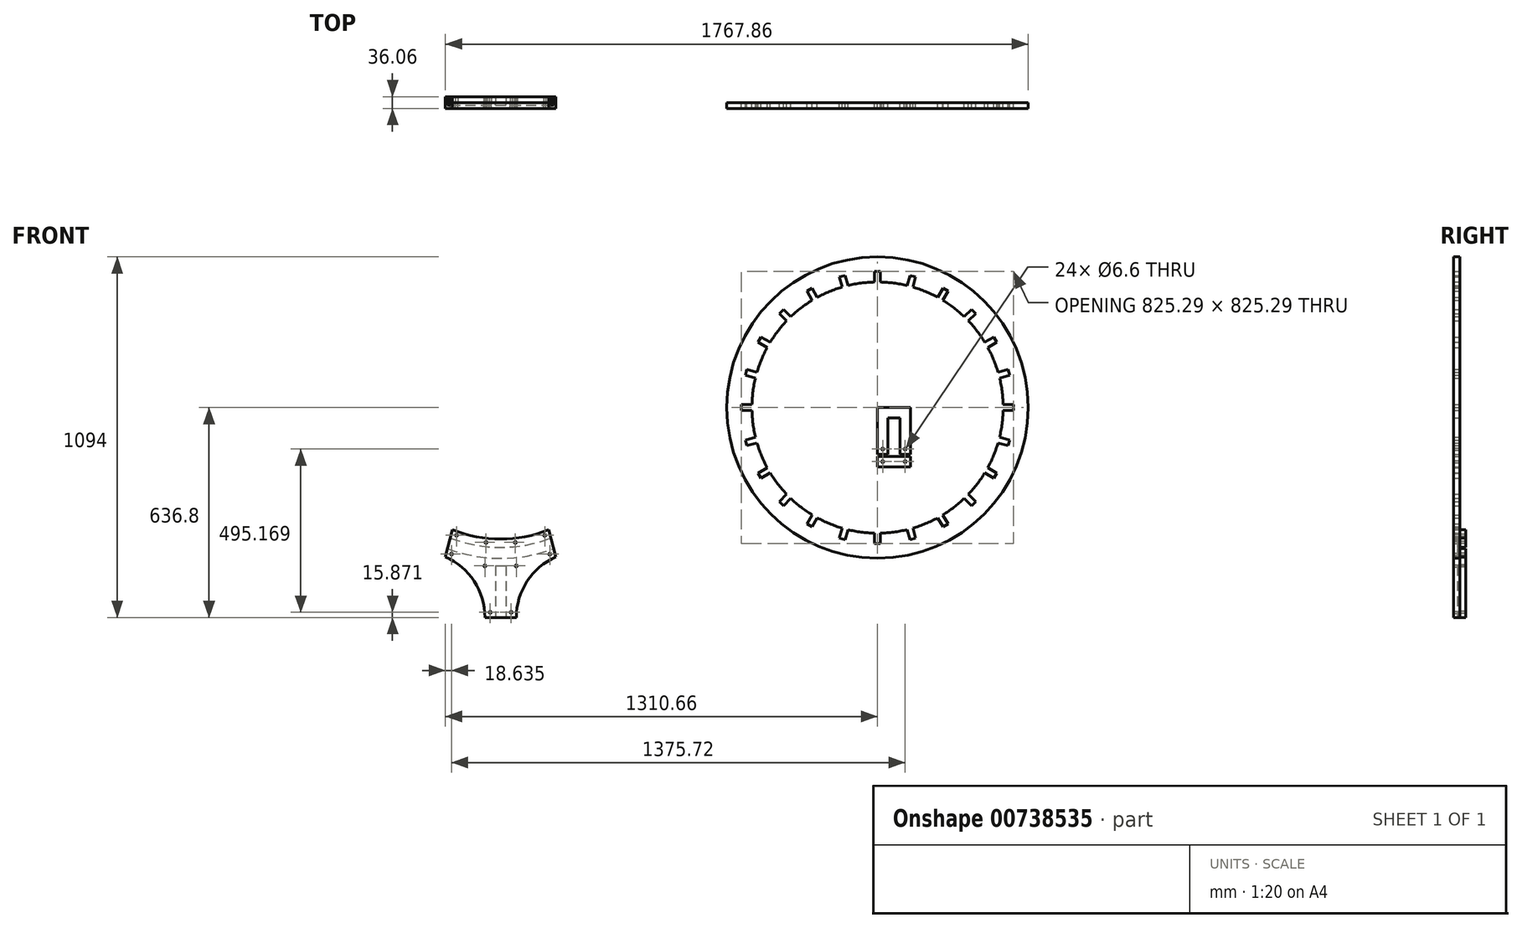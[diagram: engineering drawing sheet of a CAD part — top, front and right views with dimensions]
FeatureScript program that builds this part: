
annotation { "Feature Type Name" : "Feature", "Feature Type Description" : "" }
export const myFeature = defineFeature(function(context is Context, id is Id, definition is map)
    precondition{}
    {
        {
            var Q0;
            Q0=qCreatedBy(makeId("Front.planeOp"),FACE);
            var sketch = newSketch(context, id + "F0", { "sketchPlane" : qUnion([Q0])});
            skLineSegment(sketch, "E0.bottom", {"start": v(-15.88, -456.92) * mm, "end": v(15.87, -456.92) * mm, "construction": true});
            skLineSegment(sketch, "E0.top", {"start": v(-15.87, -660.12) * mm, "end": v(15.88, -660.12) * mm, "construction": true});
            skLineSegment(sketch, "E0.left", {"start": v(-15.87, -456.92) * mm, "end": v(-15.87, -660.12) * mm, "construction": true});
            skLineSegment(sketch, "E0.right", {"start": v(15.88, -456.92) * mm, "end": v(15.88, -660.12) * mm, "construction": true});
            skPoint(sketch, "E0.middle", {"position": v(0, -558.52) * mm});
            skLineSegment(sketch, "E1", {"start": v(-152.4, -395.59) * mm, "end": v(152.4, -395.59) * mm, "construction": true});
            skPoint(sketch, "E2", {"position": v(0, -395.59) * mm});
            skLineSegment(sketch, "E3", {"start": v(-152.4, -395.59) * mm, "end": v(-161.06, -427.9) * mm});
            skLineSegment(sketch, "E4", {"start": v(0, -395.59) * mm, "end": v(0, -457.2) * mm, "construction": true});
            skLineSegment(sketch, "E5.MirrorCS", {"start": v(152.4, -395.59) * mm, "end": v(161.06, -427.9) * mm});
            skArc(sketch, "E6", {"start": v(152.4, -395.59) * mm, "mid": v(0, 423.93) * mm, "end": v(-152.4, -395.59) * mm, "construction": true});
            skArc(sketch, "E7", {"start": v(-152.4, -395.59) * mm, "mid": v(-118.62, -407) * mm, "end": v(-84, -415.52) * mm});
            skArc(sketch, "E8", {"start": v(-161.06, -427.9) * mm, "mid": v(-126.24, -439.43) * mm, "end": v(-90.6, -448.13) * mm});
            skArc(sketch, "E9", {"start": v(161.06, -427.9) * mm, "mid": v(0, 457.2) * mm, "end": v(-161.06, -427.9) * mm, "construction": true});
            skArc(sketch, "E10.0", {"start": v(-145.79, -370.9) * mm, "mid": v(0, -398.53) * mm, "end": v(145.79, -370.9) * mm});
            skArc(sketch, "E11.0", {"start": v(-167.66, -452.54) * mm, "mid": v(0, -482.6) * mm, "end": v(167.66, -452.54) * mm, "construction": true});
            skLineSegment(sketch, "E12", {"start": v(-161.06, -427.9) * mm, "end": v(-167.66, -452.54) * mm});
            skLineSegment(sketch, "E13", {"start": v(-152.4, -395.59) * mm, "end": v(-145.79, -370.9) * mm});
            skLineSegment(sketch, "E14.MirrorCS", {"start": v(152.4, -395.59) * mm, "end": v(145.79, -370.9) * mm});
            skLineSegment(sketch, "E15.MirrorCS", {"start": v(161.06, -427.9) * mm, "end": v(167.66, -452.54) * mm});
            skLineSegment(sketch, "E16.bottom", {"start": v(-47.63, -480.24) * mm, "end": v(47.62, -480.24) * mm, "construction": true});
            skLineSegment(sketch, "E16.top", {"start": v(-47.63, -636.8) * mm, "end": v(-15.87, -636.8) * mm});
            skLineSegment(sketch, "E16.left", {"start": v(-47.63, -480.24) * mm, "end": v(-47.63, -636.8) * mm, "construction": true});
            skLineSegment(sketch, "E16.right", {"start": v(47.62, -480.24) * mm, "end": v(47.62, -636.8) * mm, "construction": true});
            skArc(sketch, "E17", {"start": v(-47.62, -636.8) * mm, "mid": v(-80.28, -526.85) * mm, "end": v(-167.66, -452.54) * mm});
            skArc(sketch, "E18.MirrorCS", {"start": v(47.62, -636.8) * mm, "mid": v(80.28, -526.85) * mm, "end": v(167.66, -452.54) * mm});
            skLineSegment(sketch, "E19.bottom", {"start": v(-15.87, -480.24) * mm, "end": v(15.88, -480.24) * mm});
            skLineSegment(sketch, "E19.top", {"start": v(-15.87, -636.8) * mm, "end": v(15.88, -636.8) * mm});
            skLineSegment(sketch, "E19.left", {"start": v(-15.87, -480.24) * mm, "end": v(-15.87, -636.8) * mm});
            skLineSegment(sketch, "E19.right", {"start": v(15.88, -480.24) * mm, "end": v(15.88, -636.8) * mm});
            skArc(sketch, "E20", {"start": v(-84, -415.52) * mm, "mid": v(35.62, -422.43) * mm, "end": v(152.4, -395.59) * mm});
            skArc(sketch, "E21", {"start": v(-90.6, -448.13) * mm, "mid": v(36.65, -455.73) * mm, "end": v(161.06, -427.9) * mm});
            skLineSegment(sketch, "E22", {"start": v(-149.1, -383.24) * mm, "end": v(-133.76, -387.35) * mm, "construction": true});
            skLineSegment(sketch, "E23", {"start": v(-164.36, -440.22) * mm, "end": v(-149.02, -444.33) * mm, "construction": true});
            skCircle(sketch, "E24", {"center": v(-133.76, -387.35) * mm, "radius": 3.3 * mm});
            skCircle(sketch, "E25", {"center": v(-149.02, -444.33) * mm, "radius": 3.3 * mm});
            skCircle(sketch, "E26.MirrorC", {"center": v(133.76, -387.35) * mm, "radius": 3.3 * mm});
            skCircle(sketch, "E27.MirrorC", {"center": v(149.02, -444.33) * mm, "radius": 3.3 * mm});
            skLineSegment(sketch, "E28", {"start": v(15.88, -636.8) * mm, "end": v(47.62, -636.8) * mm});
            skArc(sketch, "E29.0", {"start": v(-44.45, -408.82) * mm, "mid": v(0, -411.23) * mm, "end": v(44.45, -408.82) * mm, "construction": true});
            skPoint(sketch, "E30", {"position": v(0, -411.23) * mm});
            skCircle(sketch, "E31", {"center": v(44.45, -408.82) * mm, "radius": 3.3 * mm});
            skCircle(sketch, "E32", {"center": v(-44.45, -408.82) * mm, "radius": 3.3 * mm});
            skCircle(sketch, "E33", {"center": v(47.62, -480.24) * mm, "radius": 3.3 * mm});
            skCircle(sketch, "E34", {"center": v(-47.63, -480.24) * mm, "radius": 3.3 * mm});
            skLineSegment(sketch, "E35", {"start": v(-31.75, -636.8) * mm, "end": v(-31.75, -620.93) * mm, "construction": true});
            skCircle(sketch, "E36", {"center": v(-31.75, -620.93) * mm, "radius": 3.3 * mm});
            skCircle(sketch, "E37.MirrorC", {"center": v(31.75, -620.93) * mm, "radius": 3.3 * mm});
            skCircle(sketch, "E38", {"center": v(1143, 0) * mm, "radius": 457.2 * mm});
            skCircle(sketch, "E39", {"center": v(1143, 0) * mm, "radius": 381 * mm});
            skLineSegment(sketch, "E40", {"start": v(1143, 457.2) * mm, "end": v(1143, 381) * mm, "construction": true});
            skLineSegment(sketch, "E41.bottom", {"start": v(1133.98, 380.9) * mm, "end": v(1152.02, 380.9) * mm});
            skLineSegment(sketch, "E41.top", {"start": v(1133.98, 412.64) * mm, "end": v(1152.02, 412.64) * mm});
            skLineSegment(sketch, "E41.left", {"start": v(1133.98, 380.9) * mm, "end": v(1133.98, 412.64) * mm});
            skLineSegment(sketch, "E41.right", {"start": v(1152.02, 380.9) * mm, "end": v(1152.02, 412.64) * mm});
            skPoint(sketch, "E42", {"position": v(1143, 380.9) * mm});
            skLineSegment(sketch, "E43.bottom", {"start": v(1143, 0) * mm, "end": v(1242.57, 0) * mm});
            skLineSegment(sketch, "E43.top", {"start": v(1143, -109.89) * mm, "end": v(1242.57, -109.89) * mm, "construction": true});
            skLineSegment(sketch, "E43.left", {"start": v(1143, 0) * mm, "end": v(1143, -109.89) * mm});
            skLineSegment(sketch, "E43.right", {"start": v(1242.57, 0) * mm, "end": v(1242.57, -109.89) * mm});
            skLineSegment(sketch, "E44.bottom", {"start": v(1174.75, -109.89) * mm, "end": v(1210.82, -109.89) * mm});
            skLineSegment(sketch, "E44.top", {"start": v(1174.75, -31.75) * mm, "end": v(1210.82, -31.75) * mm});
            skLineSegment(sketch, "E44.left", {"start": v(1174.75, -109.89) * mm, "end": v(1174.75, -31.75) * mm});
            skLineSegment(sketch, "E44.right", {"start": v(1210.82, -109.89) * mm, "end": v(1210.82, -31.75) * mm});
            skPoint(sketch, "E44.middle", {"position": v(1192.78, -70.82) * mm});
            skPoint(sketch, "E44.middle.positionSnap0", {"position": v(1192.78, -109.89) * mm});
            skPoint(sketch, "E44.centerSnap0", {"position": v(1192.78, -109.89) * mm});
            skCircle(sketch, "E45.0", {"center": v(1143, 0) * mm, "radius": 490.78 * mm, "construction": true});
            skLineSegment(sketch, "E46.1.0", {"start": v(1053.13, 370.25) * mm, "end": v(1044.9, 400.92) * mm});
            skLineSegment(sketch, "E46.1.1", {"start": v(1027.5, 396.25) * mm, "end": v(1044.9, 400.92) * mm});
            skLineSegment(sketch, "E46.1.2", {"start": v(1035.7, 365.58) * mm, "end": v(1027.5, 396.25) * mm});
            skLineSegment(sketch, "E46.2.0", {"start": v(960.36, 334.37) * mm, "end": v(944.49, 361.87) * mm});
            skLineSegment(sketch, "E46.2.1", {"start": v(928.87, 352.85) * mm, "end": v(944.49, 361.87) * mm});
            skLineSegment(sketch, "E46.2.2", {"start": v(944.74, 325.35) * mm, "end": v(928.87, 352.85) * mm});
            skLineSegment(sketch, "E46.3.0", {"start": v(880.04, 275.7) * mm, "end": v(857.6, 298.16) * mm});
            skLineSegment(sketch, "E46.3.1", {"start": v(844.84, 285.4) * mm, "end": v(857.6, 298.16) * mm});
            skLineSegment(sketch, "E46.3.2", {"start": v(867.3, 262.96) * mm, "end": v(844.84, 285.4) * mm});
            skLineSegment(sketch, "E46.4.0", {"start": v(817.65, 198.26) * mm, "end": v(790.15, 214.13) * mm});
            skLineSegment(sketch, "E46.4.1", {"start": v(781.13, 198.51) * mm, "end": v(790.15, 214.13) * mm});
            skLineSegment(sketch, "E46.4.2", {"start": v(808.63, 182.64) * mm, "end": v(781.13, 198.51) * mm});
            skLineSegment(sketch, "E46.5.0", {"start": v(777.42, 107.3) * mm, "end": v(746.75, 115.5) * mm});
            skLineSegment(sketch, "E46.5.1", {"start": v(742.08, 98.1) * mm, "end": v(746.75, 115.5) * mm});
            skLineSegment(sketch, "E46.5.2", {"start": v(772.75, 89.87) * mm, "end": v(742.08, 98.1) * mm});
            skLineSegment(sketch, "E46.6.0", {"start": v(762.1, 9.02) * mm, "end": v(730.36, 9.02) * mm});
            skLineSegment(sketch, "E46.6.1", {"start": v(730.36, -9.02) * mm, "end": v(730.36, 9.02) * mm});
            skLineSegment(sketch, "E46.6.2", {"start": v(762.1, -9.02) * mm, "end": v(730.36, -9.02) * mm});
            skLineSegment(sketch, "E46.7.0", {"start": v(772.75, -89.87) * mm, "end": v(742.08, -98.1) * mm});
            skLineSegment(sketch, "E46.7.1", {"start": v(746.75, -115.5) * mm, "end": v(742.08, -98.1) * mm});
            skLineSegment(sketch, "E46.7.2", {"start": v(777.42, -107.3) * mm, "end": v(746.75, -115.5) * mm});
            skLineSegment(sketch, "E46.8.0", {"start": v(808.63, -182.64) * mm, "end": v(781.13, -198.51) * mm});
            skLineSegment(sketch, "E46.8.1", {"start": v(790.15, -214.13) * mm, "end": v(781.13, -198.51) * mm});
            skLineSegment(sketch, "E46.8.2", {"start": v(817.65, -198.26) * mm, "end": v(790.15, -214.13) * mm});
            skLineSegment(sketch, "E46.9.0", {"start": v(867.3, -262.96) * mm, "end": v(844.84, -285.4) * mm});
            skLineSegment(sketch, "E46.9.1", {"start": v(857.6, -298.16) * mm, "end": v(844.84, -285.4) * mm});
            skLineSegment(sketch, "E46.9.2", {"start": v(880.04, -275.7) * mm, "end": v(857.6, -298.16) * mm});
            skLineSegment(sketch, "E46.10.0", {"start": v(944.74, -325.35) * mm, "end": v(928.87, -352.85) * mm});
            skLineSegment(sketch, "E46.10.1", {"start": v(944.49, -361.87) * mm, "end": v(928.87, -352.85) * mm});
            skLineSegment(sketch, "E46.10.2", {"start": v(960.36, -334.37) * mm, "end": v(944.49, -361.87) * mm});
            skLineSegment(sketch, "E46.11.0", {"start": v(1035.7, -365.58) * mm, "end": v(1027.5, -396.25) * mm});
            skLineSegment(sketch, "E46.11.1", {"start": v(1044.9, -400.92) * mm, "end": v(1027.5, -396.25) * mm});
            skLineSegment(sketch, "E46.11.2", {"start": v(1053.13, -370.25) * mm, "end": v(1044.9, -400.92) * mm});
            skLineSegment(sketch, "E46.12.0", {"start": v(1133.98, -380.9) * mm, "end": v(1133.98, -412.64) * mm});
            skLineSegment(sketch, "E46.12.1", {"start": v(1152.02, -412.64) * mm, "end": v(1133.98, -412.64) * mm});
            skLineSegment(sketch, "E46.12.2", {"start": v(1152.02, -380.9) * mm, "end": v(1152.02, -412.64) * mm});
            skLineSegment(sketch, "E46.13.0", {"start": v(1232.87, -370.25) * mm, "end": v(1241.1, -400.92) * mm});
            skLineSegment(sketch, "E46.13.1", {"start": v(1258.5, -396.25) * mm, "end": v(1241.1, -400.92) * mm});
            skLineSegment(sketch, "E46.13.2", {"start": v(1250.3, -365.58) * mm, "end": v(1258.5, -396.25) * mm});
            skLineSegment(sketch, "E46.14.0", {"start": v(1325.64, -334.37) * mm, "end": v(1341.51, -361.87) * mm});
            skLineSegment(sketch, "E46.14.1", {"start": v(1357.13, -352.85) * mm, "end": v(1341.51, -361.87) * mm});
            skLineSegment(sketch, "E46.14.2", {"start": v(1341.26, -325.35) * mm, "end": v(1357.13, -352.85) * mm});
            skLineSegment(sketch, "E46.15.0", {"start": v(1405.96, -275.7) * mm, "end": v(1428.4, -298.16) * mm});
            skLineSegment(sketch, "E46.15.1", {"start": v(1441.16, -285.4) * mm, "end": v(1428.4, -298.16) * mm});
            skLineSegment(sketch, "E46.15.2", {"start": v(1418.7, -262.96) * mm, "end": v(1441.16, -285.4) * mm});
            skLineSegment(sketch, "E46.16.0", {"start": v(1468.35, -198.26) * mm, "end": v(1495.85, -214.13) * mm});
            skLineSegment(sketch, "E46.16.1", {"start": v(1504.87, -198.51) * mm, "end": v(1495.85, -214.13) * mm});
            skLineSegment(sketch, "E46.16.2", {"start": v(1477.37, -182.64) * mm, "end": v(1504.87, -198.51) * mm});
            skLineSegment(sketch, "E46.17.0", {"start": v(1508.58, -107.3) * mm, "end": v(1539.25, -115.5) * mm});
            skLineSegment(sketch, "E46.17.1", {"start": v(1543.92, -98.1) * mm, "end": v(1539.25, -115.5) * mm});
            skLineSegment(sketch, "E46.17.2", {"start": v(1513.25, -89.87) * mm, "end": v(1543.92, -98.1) * mm});
            skLineSegment(sketch, "E46.18.0", {"start": v(1523.9, -9.02) * mm, "end": v(1555.64, -9.02) * mm});
            skLineSegment(sketch, "E46.18.1", {"start": v(1555.64, 9.02) * mm, "end": v(1555.64, -9.02) * mm});
            skLineSegment(sketch, "E46.18.2", {"start": v(1523.9, 9.02) * mm, "end": v(1555.64, 9.02) * mm});
            skLineSegment(sketch, "E46.19.0", {"start": v(1513.25, 89.87) * mm, "end": v(1543.92, 98.1) * mm});
            skLineSegment(sketch, "E46.19.1", {"start": v(1539.25, 115.5) * mm, "end": v(1543.92, 98.1) * mm});
            skLineSegment(sketch, "E46.19.2", {"start": v(1508.58, 107.3) * mm, "end": v(1539.25, 115.5) * mm});
            skLineSegment(sketch, "E46.20.0", {"start": v(1477.37, 182.64) * mm, "end": v(1504.87, 198.51) * mm});
            skLineSegment(sketch, "E46.20.1", {"start": v(1495.85, 214.13) * mm, "end": v(1504.87, 198.51) * mm});
            skLineSegment(sketch, "E46.20.2", {"start": v(1468.35, 198.26) * mm, "end": v(1495.85, 214.13) * mm});
            skLineSegment(sketch, "E46.21.0", {"start": v(1418.7, 262.96) * mm, "end": v(1441.16, 285.4) * mm});
            skLineSegment(sketch, "E46.21.1", {"start": v(1428.4, 298.16) * mm, "end": v(1441.16, 285.4) * mm});
            skLineSegment(sketch, "E46.21.2", {"start": v(1405.96, 275.7) * mm, "end": v(1428.4, 298.16) * mm});
            skLineSegment(sketch, "E46.22.0", {"start": v(1341.26, 325.35) * mm, "end": v(1357.13, 352.85) * mm});
            skLineSegment(sketch, "E46.22.1", {"start": v(1341.51, 361.87) * mm, "end": v(1357.13, 352.85) * mm});
            skLineSegment(sketch, "E46.22.2", {"start": v(1325.64, 334.37) * mm, "end": v(1341.51, 361.87) * mm});
            skLineSegment(sketch, "E46.23.0", {"start": v(1250.3, 365.58) * mm, "end": v(1258.5, 396.25) * mm});
            skLineSegment(sketch, "E46.23.1", {"start": v(1241.1, 400.92) * mm, "end": v(1258.5, 396.25) * mm});
            skLineSegment(sketch, "E46.23.2", {"start": v(1232.87, 370.25) * mm, "end": v(1241.1, 400.92) * mm});
            skLineSegment(sketch, "E47", {"start": v(1143, 412.64) * mm, "end": v(1143, 490.78) * mm, "construction": true});
            skLineSegment(sketch, "E48.bottom", {"start": v(1143, -109.89) * mm, "end": v(1174.75, -109.89) * mm, "construction": true});
            skLineSegment(sketch, "E48.top", {"start": v(1143, -141.64) * mm, "end": v(1174.75, -141.64) * mm});
            skLineSegment(sketch, "E48.left", {"start": v(1143, -109.89) * mm, "end": v(1143, -141.64) * mm});
            skLineSegment(sketch, "E48.right", {"start": v(1174.75, -109.89) * mm, "end": v(1174.75, -141.64) * mm});
            skLineSegment(sketch, "E49.bottom", {"start": v(1210.82, -109.89) * mm, "end": v(1242.57, -109.89) * mm, "construction": true});
            skLineSegment(sketch, "E49.top", {"start": v(1210.82, -141.64) * mm, "end": v(1242.57, -141.64) * mm});
            skLineSegment(sketch, "E49.left", {"start": v(1210.82, -109.89) * mm, "end": v(1210.82, -141.64) * mm});
            skLineSegment(sketch, "E49.right", {"start": v(1242.57, -109.89) * mm, "end": v(1242.57, -141.64) * mm});
            skCircle(sketch, "E50", {"center": v(1158.88, -125.76) * mm, "radius": 3.3 * mm});
            skPoint(sketch, "E50.centerSnap0", {"position": v(1174.75, -125.76) * mm});
            skPoint(sketch, "E50.centerSnap1", {"position": v(1158.88, -109.89) * mm});
            skCircle(sketch, "E51", {"center": v(1226.7, -125.76) * mm, "radius": 3.3 * mm});
            skPoint(sketch, "E51.centerSnap0", {"position": v(1210.82, -125.76) * mm});
            skPoint(sketch, "E51.centerSnap1", {"position": v(1226.7, -109.89) * mm});
            skLineSegment(sketch, "E52.bottom", {"start": v(1143, -147.99) * mm, "end": v(1242.57, -147.99) * mm});
            skLineSegment(sketch, "E52.top", {"start": v(1143, -179.74) * mm, "end": v(1242.57, -179.74) * mm});
            skLineSegment(sketch, "E52.left", {"start": v(1143, -147.99) * mm, "end": v(1143, -179.74) * mm});
            skLineSegment(sketch, "E52.right", {"start": v(1242.57, -147.99) * mm, "end": v(1242.57, -179.74) * mm});
            skCircle(sketch, "E53", {"center": v(1158.88, -163.86) * mm, "radius": 3.3 * mm});
            skPoint(sketch, "E53.centerSnap0", {"position": v(1143, -163.86) * mm});
            skCircle(sketch, "E54", {"center": v(1226.7, -163.86) * mm, "radius": 3.3 * mm});
            skPoint(sketch, "E54.centerSnap0", {"position": v(1226.7, -141.64) * mm});
            skPoint(sketch, "E54.centerSnap1", {"position": v(1242.57, -163.86) * mm});
            skSolve(sketch);
        }
        {
            var Q0;
            Q0=makeQuery(id+"F0.imprint","IMPRINT",FACE,{"disambiguationData":[TD([[makeQuery(id+"F0.imprint","IMPRINT",EDGE,{"derivedFrom":sQuery(id+"F0.wireOp",EDGE,"E7")}),1.0]])]});
            var Q1;
            Q1=makeQuery(id+"F0.imprint","IMPRINT",FACE,{"disambiguationData":[TD([[makeQuery(id+"F0.imprint","IMPRINT",EDGE,{"derivedFrom":sQuery(id+"F0.wireOp",EDGE,"E8")}),-1.0]])]});
            var Q2;
            Q2=makeQuery(id+"F0.imprint","IMPRINT",FACE,{"disambiguationData":[TD([[makeQuery(id+"F0.imprint","IMPRINT",EDGE,{"derivedFrom":sQuery(id+"F0.wireOp",EDGE,"E38")}),1.0]])]});
            var Q3;
            Q3=makeQuery(id+"F0.imprint","IMPRINT",FACE,{"disambiguationData":[TD([[makeQuery(id+"F0.imprint","IMPRINT",EDGE,{"derivedFrom":sQuery(id+"F0.wireOp",EDGE,"E43.bottom")}),-1.0]])]});
            var Q4;
            Q4=makeQuery(id+"F0.imprint","IMPRINT",FACE,{"disambiguationData":[TD([[makeQuery(id+"F0.imprint","IMPRINT",EDGE,{"derivedFrom":sQuery(id+"F0.wireOp",EDGE,"E52.bottom")}),-1.0]])]});
            extrude(context, id + "F1", {"entities" : qUnion([Q0, Q1, Q2, Q3, Q4]), "depth" : 18.03 * mm, "offsetDistance" : 25.4 * mm});
        }
        {
            var Q0;
            Q0=makeQuery(id+"F0.imprint","IMPRINT",FACE,{"disambiguationData":[TD([[makeQuery(id+"F0.imprint","IMPRINT",EDGE,{"derivedFrom":sQuery(id+"F0.wireOp",EDGE,"E7")}),1.0]])]});
            var Q1;
            Q1=makeQuery(id+"F0.imprint","IMPRINT",FACE,{"disambiguationData":[TD([[makeQuery(id+"F0.imprint","IMPRINT",EDGE,{"derivedFrom":sQuery(id+"F0.wireOp",EDGE,"E8")}),-1.0]])]});
            extrude(context, id + "F2", {"entities" : qUnion([Q0, Q1]), "oppositeDirection" : true, "depth" : 18.03 * mm, "offsetDistance" : 25.4 * mm});
        }
        {
            var Q0;
            Q0=makeQuery(id+"F0.imprint","IMPRINT",FACE,{"disambiguationData":[TD([[makeQuery(id+"F0.imprint","IMPRINT",EDGE,{"derivedFrom":sQuery(id+"F0.wireOp",EDGE,"E3")}),1.0]])]});
            var Q1;
            Q1=makeQuery(id+"F0.imprint","IMPRINT",FACE,{"disambiguationData":[TD([[makeQuery(id+"F0.imprint","IMPRINT",EDGE,{"derivedFrom":sQuery(id+"F0.wireOp",EDGE,"E5.MirrorCS")}),-1.0]])]});
            var Q2;
            Q2=makeQuery(id+"F0.imprint","IMPRINT",FACE,{"disambiguationData":[TD([[makeQuery(id+"F0.imprint","IMPRINT",EDGE,{"derivedFrom":sQuery(id+"F0.wireOp",EDGE,"E19.bottom")}),-1.0]])]});
            extrude(context, id + "F3", {"entities" : qUnion([Q0, Q1, Q2]), "operationType" : NewBodyOperationType.ADD, "depth" : 18.03 * mm, "offsetDistance" : 25.4 * mm, "hasSecondDirection" : true, "secondDirectionOppositeDirection" : false, "secondDirectionDepth" : 7.37 * mm});
        }
    });
